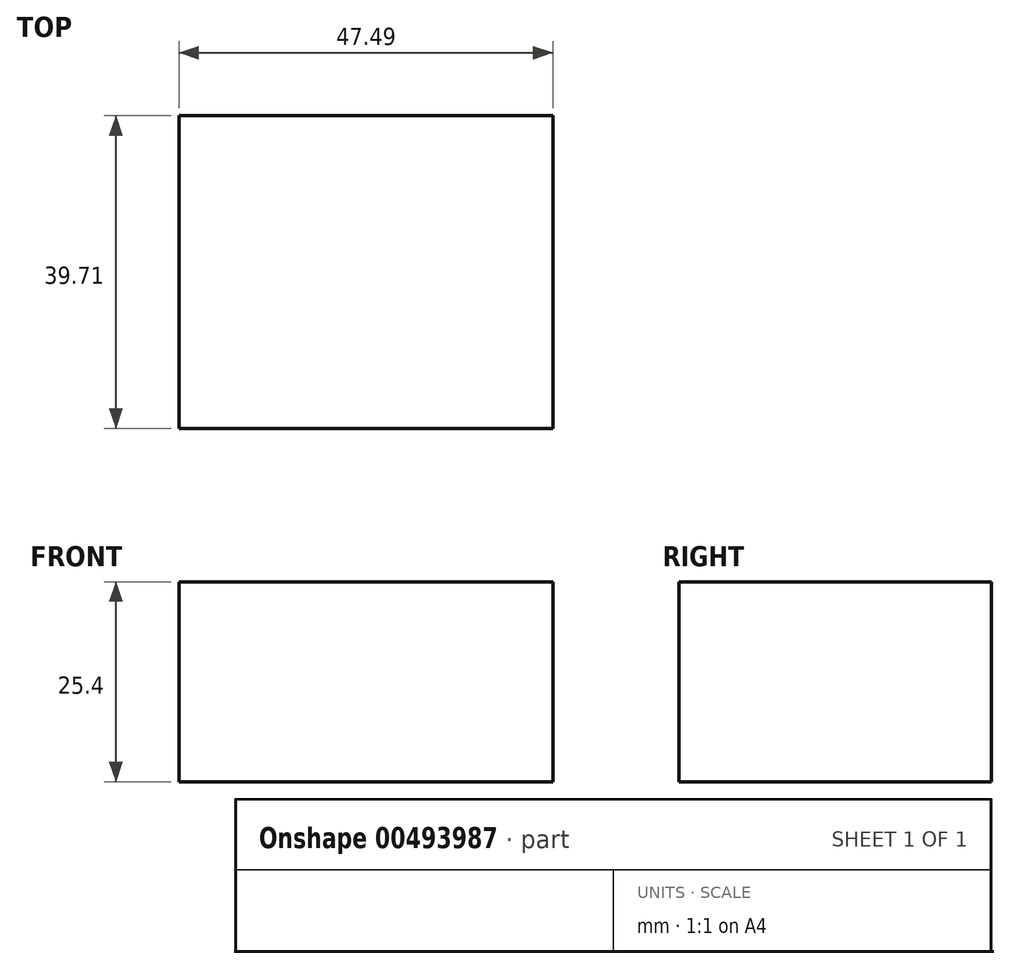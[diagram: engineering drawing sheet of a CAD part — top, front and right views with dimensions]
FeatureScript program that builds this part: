
annotation { "Feature Type Name" : "Feature", "Feature Type Description" : "" }
export const myFeature = defineFeature(function(context is Context, id is Id, definition is map)
    precondition{}
    {
        {
            var Q0;
            Q0=qCreatedBy(makeId("Top.planeOp"),FACE);
            var sketch = newSketch(context, id + "F0", { "sketchPlane" : qUnion([Q0])});
            skLineSegment(sketch, "E0.bottom", {"start": v(11.75, 55.11) * mm, "end": v(59.24, 55.11) * mm});
            skLineSegment(sketch, "E0.top", {"start": v(11.75, 15.4) * mm, "end": v(59.24, 15.4) * mm});
            skLineSegment(sketch, "E0.left", {"start": v(11.75, 55.11) * mm, "end": v(11.75, 15.4) * mm});
            skLineSegment(sketch, "E0.right", {"start": v(59.24, 55.11) * mm, "end": v(59.24, 15.4) * mm});
            skSolve(sketch);
        }
        {
            var Q0;
            Q0 = qSketchRegion(id + "F0", true);
            extrude(context, id + "F1", {"entities" : qUnion([Q0]), "depth" : 25.4 * mm});
        }
    });
